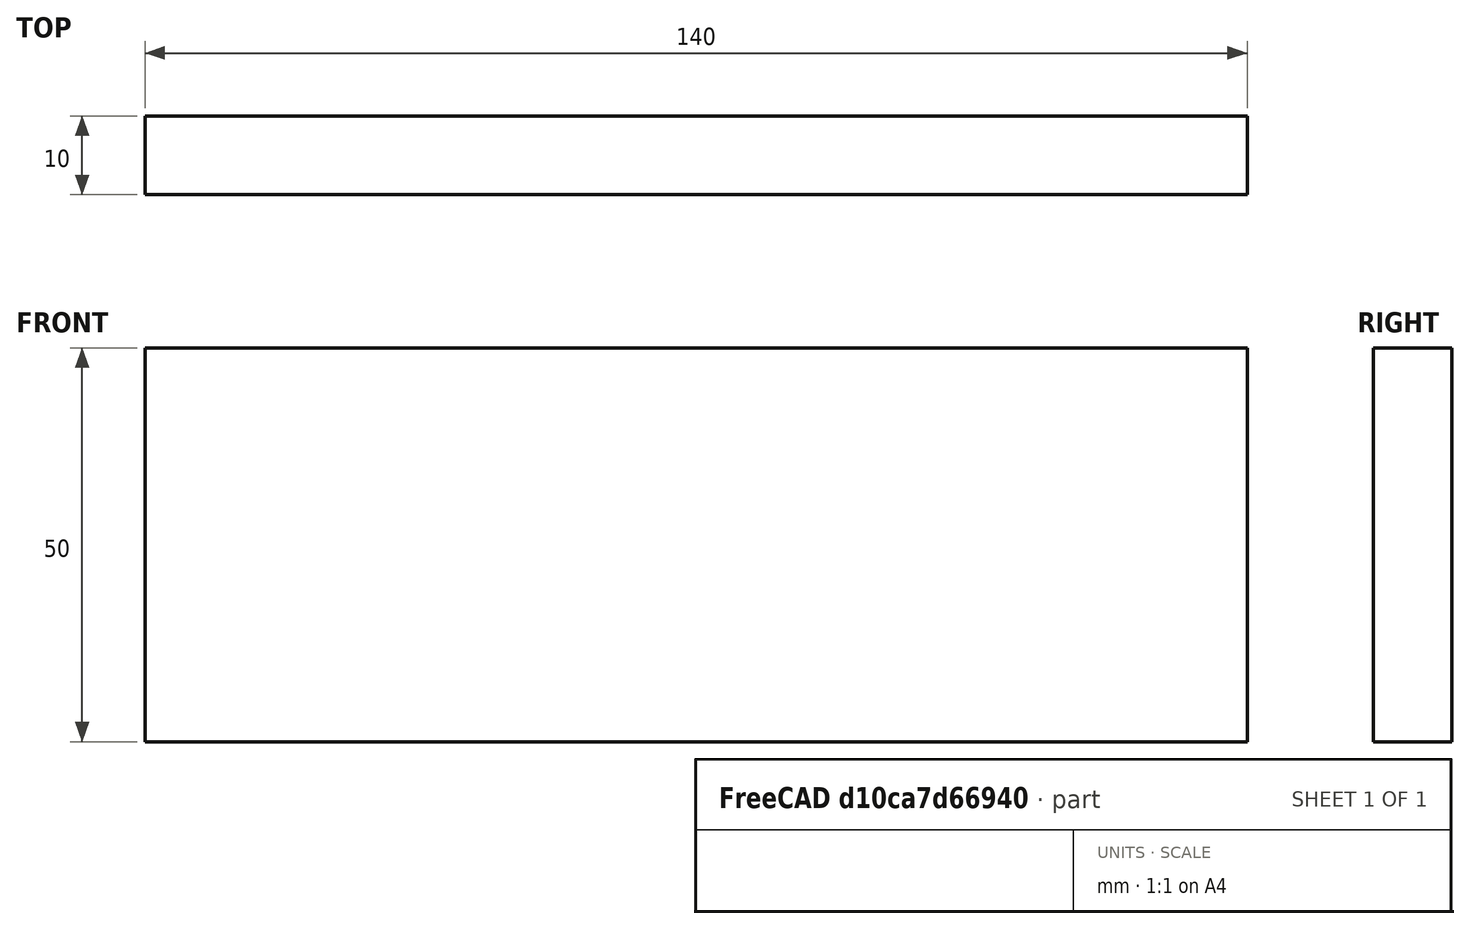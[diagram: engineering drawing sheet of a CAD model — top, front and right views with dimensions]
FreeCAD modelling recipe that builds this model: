
FCSTD DOCUMENT  (FreeCAD 0.15R4671 (Git))
Label: Flat Bar 140x10 EN10058 S235JR
License: All rights reserved
LicenseURL: http://en.wikipedia.org/wiki/All_rights_reserved
objects: Sketcher::SketchObject×1, Part::Extrusion×1
note: 2 computed .brp shape members not serialized (recipe doc carries the construction recipe); baked Part::Feature solids carry a one-line shape summary decoded from their .brp

FEATURE [Sketcher::SketchObject] Sketch
  sketch-geometry (4):
    g0: LineSegment StartX=-70 StartY=-5 StartZ=0 EndX=70 EndY=-5 EndZ=0
    g1: LineSegment StartX=70 StartY=-5 StartZ=0 EndX=70 EndY=5 EndZ=0
    g2: LineSegment StartX=70 StartY=5 StartZ=0 EndX=-70 EndY=5 EndZ=0
    g3: LineSegment StartX=-70 StartY=5 StartZ=0 EndX=-70 EndY=-5 EndZ=0
  constraints (12):
    c: Coincident(g0,g1)
    c: Coincident(g1,g2)
    c: Coincident(g2,g3)
    c: Coincident(g3,g0)
    c: Horizontal(g0)
    c: Horizontal(g2)
    c: Vertical(g1)
    c: Vertical(g3)
    c: Symmetric(g1,g2,g-2)
    c: Symmetric(g0,g1,g-1)
    c: DistanceY(g1) = 10
    c: DistanceX(g0) = 140
FEATURE [Part::Extrusion] Extrude  label="Flat Bar 140x10 EN10058 S235JR"
  Base = -> Sketch
  Dir = (0,0,50)
  Solid = true
